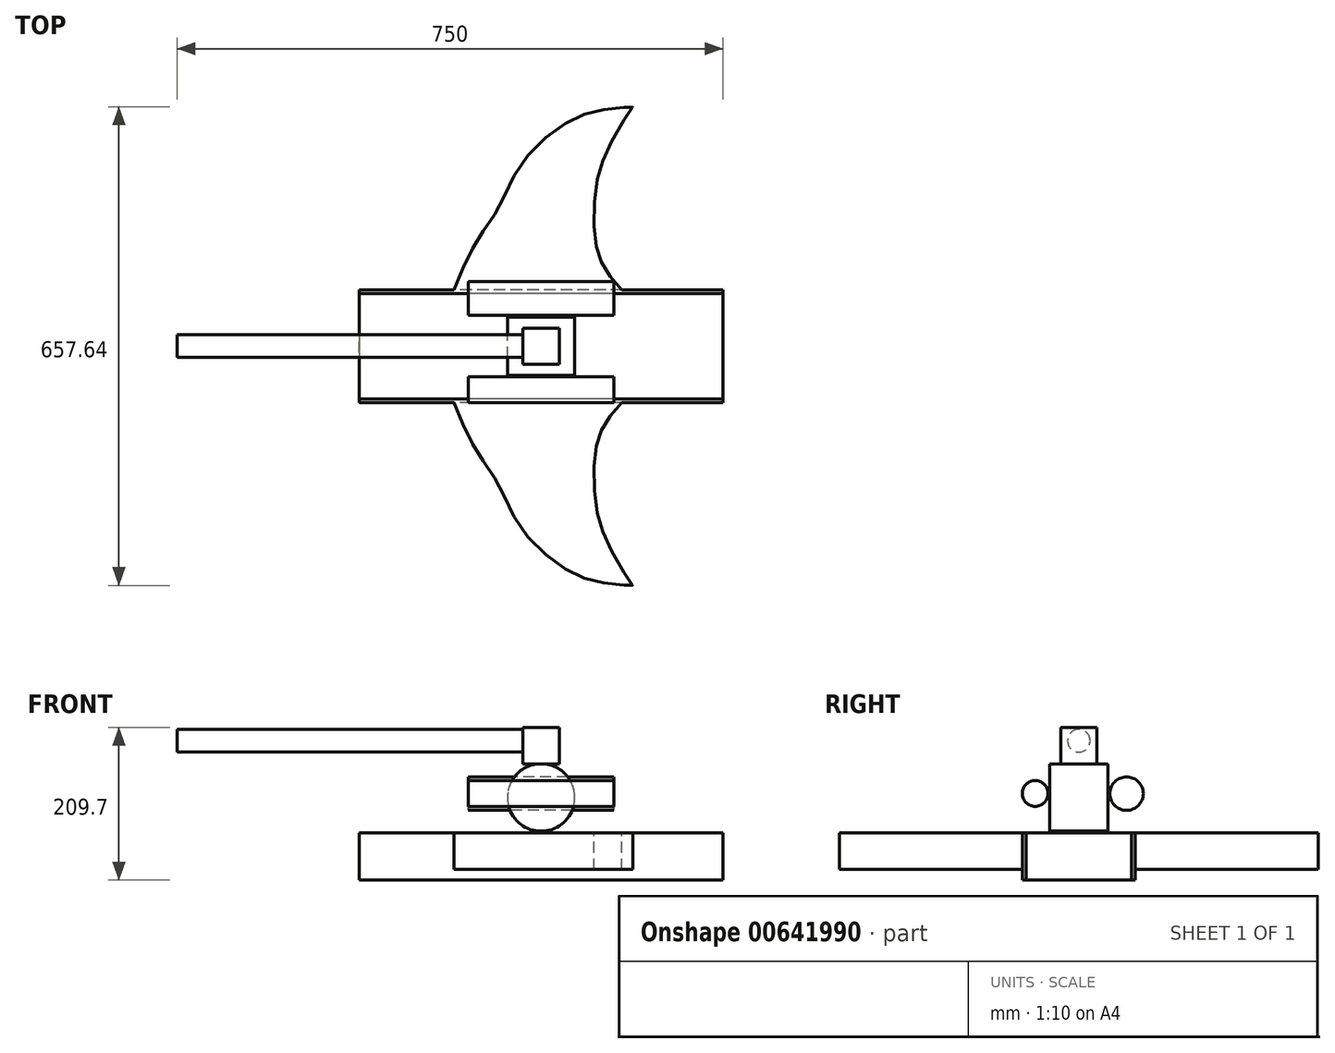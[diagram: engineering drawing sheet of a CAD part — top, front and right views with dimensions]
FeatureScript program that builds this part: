
annotation { "Feature Type Name" : "Feature", "Feature Type Description" : "" }
export const myFeature = defineFeature(function(context is Context, id is Id, definition is map)
    precondition{}
    {
        {
            var Q0;
            Q0=qCreatedBy(makeId("Top.planeOp"),FACE);
            var sketch = newSketch(context, id + "F0", { "sketchPlane" : qUnion([Q0])});
            skLineSegment(sketch, "E0.bottom", {"start": v(25, 25) * mm, "end": v(-25, 25) * mm});
            skLineSegment(sketch, "E0.top", {"start": v(25, -25) * mm, "end": v(-25, -25) * mm});
            skLineSegment(sketch, "E0.left", {"start": v(25, 25) * mm, "end": v(25, -25) * mm});
            skLineSegment(sketch, "E0.right", {"start": v(-25, 25) * mm, "end": v(-25, -25) * mm});
            skPoint(sketch, "E0.middle", {"position": v(0, 0) * mm});
            skSolve(sketch);
        }
        {
            var Q0;
            Q0 = qSketchRegion(id + "F0", true);
            extrude(context, id + "F1", {"entities" : qUnion([Q0]), "depth" : 50 * mm, "offsetDistance" : 25 * mm});
        }
        {
            var Q0;
            Q0=qCreatedBy(makeId("Front.planeOp"),FACE);
            var sketch = newSketch(context, id + "F2", { "sketchPlane" : qUnion([Q0])});
            skCircle(sketch, "E1", {"center": v(0, -46.34) * mm, "radius": 46.34 * mm});
            skSolve(sketch);
        }
        {
            var Q0;
            Q0=makeQuery(id+"F2.imprint","IMPRINT",FACE,{"disambiguationData":[TD([[makeQuery(id+"F2.imprint","IMPRINT",EDGE,{"derivedFrom":sQuery(id+"F2.wireOp",EDGE,"E1")}),1.0]])]});
            extrude(context, id + "F3", {"entities" : qUnion([Q0]), "operationType" : NewBodyOperationType.ADD, "endBound" : BoundingType.SYMMETRIC, "depth" : 80 * mm, "offsetDistance" : 25 * mm});
        }
        {
            var Q0;
            Q0=qCreatedBy(makeId("Right.planeOp"),FACE);
            var sketch = newSketch(context, id + "F4", { "sketchPlane" : qUnion([Q0])});
            skCircle(sketch, "E2", {"center": v(-60.02, -40.82) * mm, "radius": 17.73 * mm});
            skCircle(sketch, "E3", {"center": v(65.59, -41.03) * mm, "radius": 22.99 * mm});
            skSolve(sketch);
        }
        {
            var Q0;
            Q0 = qSketchRegion(id + "F4", true);
            extrude(context, id + "F5", {"entities" : qUnion([Q0]), "endBound" : BoundingType.SYMMETRIC, "depth" : 200 * mm, "offsetDistance" : 25 * mm});
        }
        {
            var Q0;
            Q0=qCreatedBy(makeId("Right.planeOp"),FACE);
            var sketch = newSketch(context, id + "F6", { "sketchPlane" : qUnion([Q0])});
            skLineSegment(sketch, "E4.bottom", {"start": v(77.52, -95.17) * mm, "end": v(-72.49, -95.17) * mm});
            skLineSegment(sketch, "E4.top", {"start": v(77.52, -159.7) * mm, "end": v(-72.49, -159.7) * mm});
            skLineSegment(sketch, "E4.left", {"start": v(77.52, -95.17) * mm, "end": v(77.52, -159.7) * mm});
            skLineSegment(sketch, "E4.right", {"start": v(-72.49, -95.17) * mm, "end": v(-72.49, -159.7) * mm});
            skSolve(sketch);
        }
        {
            var Q0;
            Q0=makeQuery(id+"F6.imprint","IMPRINT",FACE,{"disambiguationData":[TD([[makeQuery(id+"F6.imprint","IMPRINT",EDGE,{"derivedFrom":sQuery(id+"F6.wireOp",EDGE,"E4.bottom")}),1.0]])]});
            extrude(context, id + "F7", {"entities" : qUnion([Q0]), "endBound" : BoundingType.SYMMETRIC, "depth" : 500 * mm, "offsetDistance" : 25 * mm});
        }
        {
            var Q0;
            Q0=makeQuery(id+"F7.opExtrude","SWEPT_FACE",FACE,{"disambiguationData":[OSD([sQuery(id+"F6.wireOp",EDGE,"E4.bottom")])]});
            var sketch = newSketch(context, id + "F8", { "sketchPlane" : qUnion([Q0])});
            skFitSpline(sketch, "E5", {"points": [v(-119.88, 77.52) * mm, v(-90.7, 140.66) * mm, v(-59.15, 189.17) * mm, v(-25.63, 252.65) * mm, v(37.86, 308.65) * mm, v(91.88, 326) * mm, v(125.8, 328.76) * mm, v(125.4, 328.36) * mm, v(96.22, 279.47) * mm, v(76.5, 225.84) * mm, v(73.74, 150.52) * mm, v(85.17, 110.7) * mm, v(110.8, 77.52) * mm], "startDerivative": vector(274.37, 674.66) * mm, "endDerivative": vector(374.65, -424.96) * mm});
            skSolve(sketch);
        }
        {
            var Q0;
            {var subQ0=sQuery(id+"F8.wireOp",EDGE,"E5");Q0=makeQuery(id+"F8.imprint","IMPRINT",FACE,{"disambiguationData":[TD([[makeQuery(id+"F8.imprint","IMPRINT",EDGE,{"derivedFrom":subQ0}),-1.0]])]});}
            extrude(context, id + "F9", {"entities" : qUnion([Q0]), "operationType" : NewBodyOperationType.ADD, "oppositeDirection" : true, "depth" : 50 * mm, "offsetDistance" : 25 * mm});
        }
        {
            var Q0;
            Q0=makeQuery(id+"F7.opExtrude","SWEPT_BODY",BODY,{"disambiguationData":[OSD([sQuery(id+"F6.wireOp",EDGE,"E4.bottom"),sQuery(id+"F6.wireOp",EDGE,"E4.top"),sQuery(id+"F6.wireOp",EDGE,"E4.left"),sQuery(id+"F6.wireOp",EDGE,"E4.right")])]});
            var Q1;
            Q1=qCreatedBy(makeId("Front.planeOp"),FACE);
            mirror(context, id + "F10", {"operationType" : NewBodyOperationType.ADD, "entities" : qUnion([Q0]), "mirrorPlane" : qUnion([Q1])});
        }
        {
            var Q0;
            Q0=qCreatedBy(makeId("Right.planeOp"),FACE);
            var sketch = newSketch(context, id + "F11", { "sketchPlane" : qUnion([Q0])});
            skCircle(sketch, "E6", {"center": v(0, 31.73) * mm, "radius": 15.57 * mm});
            skSolve(sketch);
        }
        {
            var Q0;
            Q0 = qSketchRegion(id + "F11", true);
            extrude(context, id + "F12", {"entities" : qUnion([Q0]), "operationType" : NewBodyOperationType.ADD, "oppositeDirection" : true, "depth" : 500 * mm, "offsetDistance" : 25 * mm});
        }
    });
